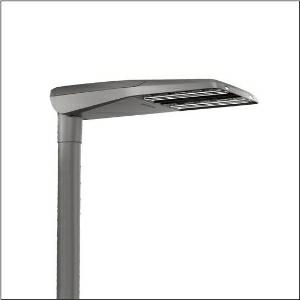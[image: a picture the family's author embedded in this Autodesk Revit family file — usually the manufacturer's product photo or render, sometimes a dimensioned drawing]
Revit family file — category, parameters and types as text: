
# Revit family: streetlight_sl_11_iq_midi___st1_2p1_0_5xc3g41f08me_0c33
name_source: partatom
category: Lighting Fixtures
units: mm (PartAtom-declared; Revit-internal decimal feet)

## family parameters
Cut with Voids When Loaded = No
Host = Face
Light Source = No
Part Type = Normal
Room Calculation Point = No
Round Connector Dimension = Use Diameter
Shared = No

## types (1)
- --- (1 x LED, 18520 lm, 121.7 W, 4000K)
    Apparent Load = 122 VA
    CIE Flux Codes = 31 68 95 100 100
    Color Rendering = 70
    Color Temperature = 4000K
    Default Elevation = 1800 mm
    Description = Streetlight SL 11 iQ midi, mast luminaire, primary light control with 3 zone facetted reflector, of plastic, silver coated, highly specular, primary optical cover: cover, of PMMA, transparent, light distribution: ST1.2P1.0, light emission: direct distribution, primary light characteristic: asymmetric, installation type: post-top, side-entry, lamps: LED, High Power LED, rated values: 18.520lm | 121,7W | 152,2lm/W (begin service life); end service life: 18.520lm | 129W; at 50% lumin. flux: 9.260lm | 56,2W | 164,8lm/W, colour temperature: 4000K, colour rendering: CRI > 70, light colour: 740, light setting 1 begin service life: 100% | 18.520lm | 121,7W | 152,2lm/W | 4.000K, light setting 1 end service life: 129W, further light settings possible, control: Street-Remote, optimised constant luminous flux control (CLO 2.0), Auto-Match, Desk-Remote (wireless, voltage-free reading and setting of iQ features in the workshop via application-optimized NFC function/RFID function), Light-Fading, Smart-Wire, Night-Set, Lumen-Switch, Temp-Guard, with cable H07RN-F 5x 1.5mm², mains connection: 230..240V, AC, 50/60Hz, connection cable pre-assembled, cable length: 12,5m, luminaire housing, of diecast aluminium, powder-coated, Siteco® metallic grey (DB 702S), please order mast flange separately, inclination adjustable without tools: 0°, 5°, 10°, 15° (post-top) | 0°, -5°, -10°, -15° (side-entry), sealing non-destructively replaceable, multi-level sealing system, length: 780mm, width: 376mm, height: 118mm, mast flange for spigot size: 42mm (side-entry): 5XC10008XM4, 60/48mm (side-entry/post-top): 5XC10108XM2, 76/60mm (side-entry/post-top): 5XC10108XM1, equipment: Power, protection rating (complete): IP66, insulation class (complete): insulation class II (safety insulation), certification: CE, ENEC, ENEC+, VDE, impact resistance: IK10, permissible operating ambient temperature for outdoor applications: -25..+50°C, standard-compliant lighting for roads and squares, Environmental Product Declaration (EPD) tested and certified by an independent institute, packaging unit: 1 piece

Light Distribution: ST1.2P1.0
    Height = 118 mm
    Lamp = 1 x LED
    Lamp Light Flux = 18520 lm
    Lamp Power = 121.7 W
    Lamp count = 1
    Length = 780 mm
    Luminous efficacy = 152 lm/W
    Manufacturer = Siteco
    ModVariant = No
    Model = 5XC3G41F08ME
    Number of Poles = 1
    OnlyDefault = Yes
    Power Factor = 1
    Product Name = Streetlight SL 11 iQ midi | ST1.2P1.0
    Product group = mast luminaire | pylon top
    ProductGroupID = 6100
    Protection Class = Protection class II
    Protection Degree = IP 66
    RLX_Detail_Level = 1
    RLX_Emergency_Light_Flux = 0 lm
    RLX_Emergency_Type = 0
    RLX_Emergency_Type_DB = No
    RlxData = <blob elided: 70965 chars, md5=a004cd1d>
    Socket = socket
    Standby Power = 0 W
    System Light Flux = 18520 lm
    System Power = 122 W
    Type Comments = factory setting: luminous flux: 100 % | dim-lin: 254 | 544 mA
    Type Image = l_1005960.jpg
    URL = http://relux.com
    VarID = @adj_037162
    Voltage = 0 V
    Weight = 0.00 kg
    Width = 376 mm

## geometry (parser evidence)
native form markers: Blend x4, Sweep x10
no freeform markers — native parametric forms only
